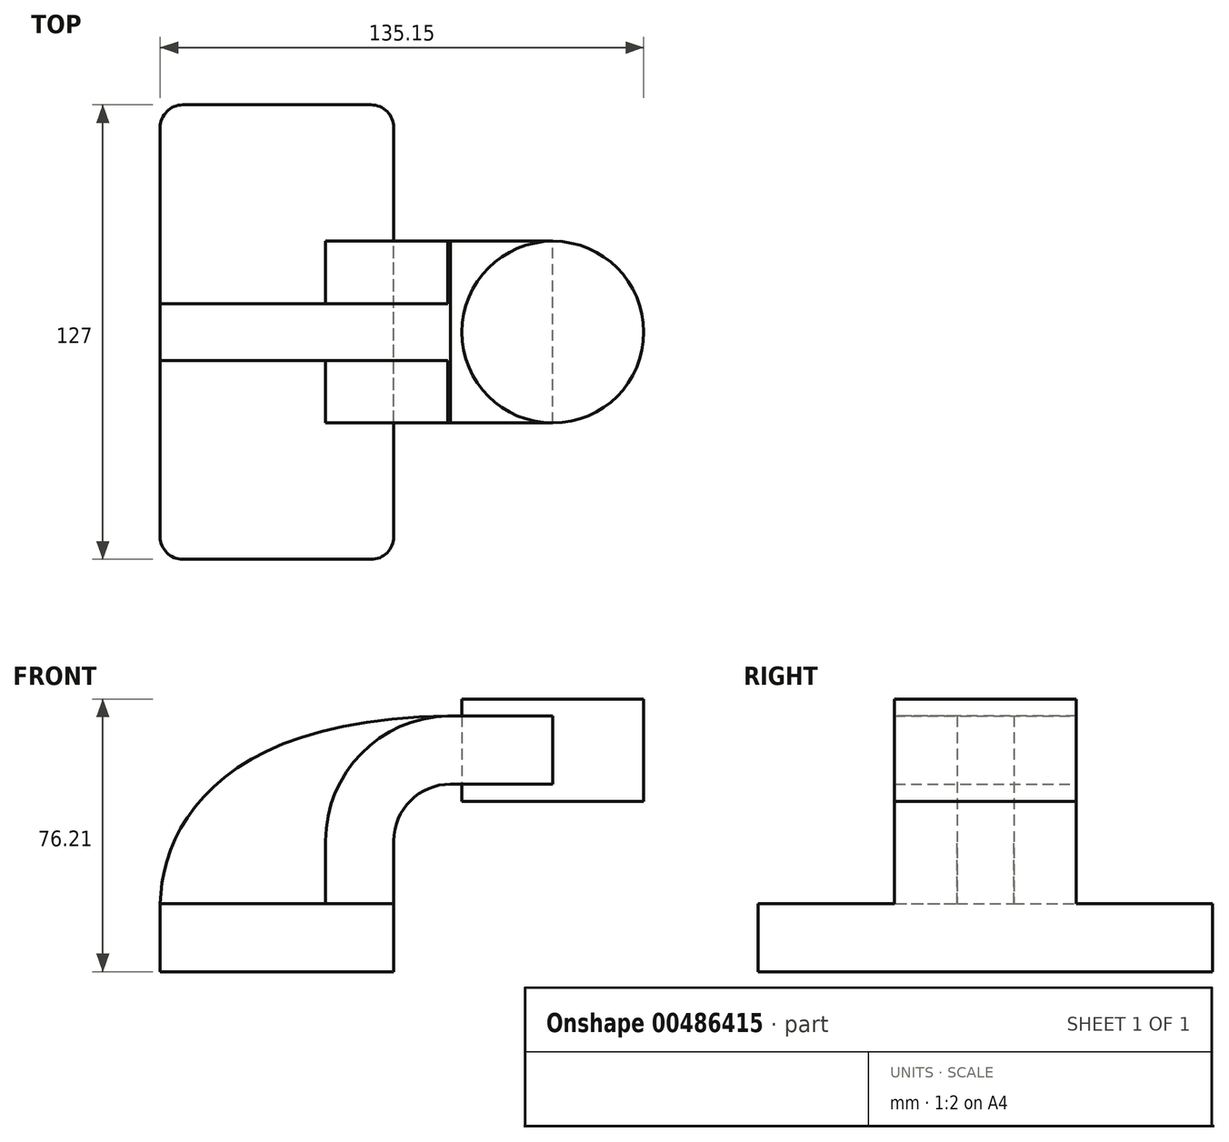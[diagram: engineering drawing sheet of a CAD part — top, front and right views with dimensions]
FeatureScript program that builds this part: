
annotation { "Feature Type Name" : "Feature", "Feature Type Description" : "" }
export const myFeature = defineFeature(function(context is Context, id is Id, definition is map)
    precondition{}
    {
        {
            var Q0;
            Q0=qCreatedBy(makeId("Front.planeOp"),FACE);
            var sketch = newSketch(context, id + "F0", { "sketchPlane" : qUnion([Q0])});
            skLineSegment(sketch, "E0.bottom", {"start": v(32.65, -9.52) * mm, "end": v(-32.65, -9.52) * mm});
            skLineSegment(sketch, "E0.top", {"start": v(32.65, 9.53) * mm, "end": v(-32.65, 9.52) * mm});
            skLineSegment(sketch, "E0.left", {"start": v(32.65, -9.52) * mm, "end": v(32.65, 9.53) * mm});
            skLineSegment(sketch, "E0.right", {"start": v(-32.65, -9.52) * mm, "end": v(-32.65, 9.53) * mm});
            skPoint(sketch, "E0.middle", {"position": v(0, 0) * mm});
            skLineSegment(sketch, "E1.bottom", {"start": v(102.5, 38.1) * mm, "end": v(51.7, 38.1) * mm});
            skLineSegment(sketch, "E1.top", {"start": v(102.5, 66.68) * mm, "end": v(51.7, 66.68) * mm});
            skLineSegment(sketch, "E1.left", {"start": v(102.5, 38.1) * mm, "end": v(102.5, 66.68) * mm});
            skLineSegment(sketch, "E1.right", {"start": v(51.7, 38.1) * mm, "end": v(51.7, 66.68) * mm});
            skPoint(sketch, "E1.middle", {"position": v(77.1, 52.39) * mm});
            skLineSegment(sketch, "E2", {"start": v(32.65, 9.53) * mm, "end": v(32.65, 27) * mm});
            skArc(sketch, "E3", {"start": v(48.52, 42.88) * mm, "mid": v(37.3, 38.23) * mm, "end": v(32.65, 27) * mm});
            skLineSegment(sketch, "E4", {"start": v(48.52, 42.88) * mm, "end": v(77.1, 42.88) * mm});
            skPoint(sketch, "E5", {"position": v(77.1, 38.1) * mm});
            skLineSegment(sketch, "E6.0", {"start": v(13.6, 9.53) * mm, "end": v(13.6, 27) * mm});
            skArc(sketch, "E6.1", {"start": v(48.52, 61.93) * mm, "mid": v(23.83, 51.7) * mm, "end": v(13.6, 27) * mm});
            skLineSegment(sketch, "E6.2", {"start": v(48.52, 61.93) * mm, "end": v(77.1, 61.93) * mm});
            skFitSpline(sketch, "E7", {"points": [v(48.52, 61.93) * mm, v(-32.65, 9.52) * mm], "startDerivative": vector(-194.04, -1.8) * mm, "endDerivative": vector(-2.1, -64.97) * mm});
            skLineSegment(sketch, "E8", {"start": v(77.1, 42.88) * mm, "end": v(77.1, 61.93) * mm});
            skLineSegment(sketch, "E9", {"start": v(77.1, 61.93) * mm, "end": v(77.1, 66.68) * mm});
            skLineSegment(sketch, "E10", {"start": v(77.1, 42.88) * mm, "end": v(77.1, 38.1) * mm});
            skSolve(sketch);
        }
        {
            var Q0;
            Q0=makeQuery(id+"F0.imprint","IMPRINT",FACE,{"disambiguationData":[TD([[makeQuery(id+"F0.imprint","IMPRINT",EDGE,{"derivedFrom":sQuery(id+"F0.wireOp",EDGE,"E0.bottom")}),-1.0]])]});
            var Q1;
            Q1=sQuery(id+"F0.wireOp",EDGE,"E0.bottom");
            var Q2;
            Q2=sQuery(id+"F0.wireOp",EDGE,"E0.left");
            var Q3;
            Q3=sQuery(id+"F0.wireOp",EDGE,"E0.right");
            var Q4;
            Q4=sQuery(id+"F0.wireOp",EDGE,"E1.bottom");
            var Q5;
            Q5=sQuery(id+"F0.wireOp",EDGE,"E1.top");
            var Q6;
            Q6=sQuery(id+"F0.wireOp",EDGE,"E1.left");
            var Q7;
            Q7=sQuery(id+"F0.wireOp",EDGE,"E1.right");
            var Q8;
            Q8=sQuery(id+"F0.wireOp",EDGE,"E2");
            var Q9;
            Q9=sQuery(id+"F0.wireOp",EDGE,"E3");
            var Q10;
            Q10=sQuery(id+"F0.wireOp",EDGE,"E4");
            var Q11;
            Q11=sQuery(id+"F0.wireOp",EDGE,"E6.0");
            var Q12;
            Q12=sQuery(id+"F0.wireOp",EDGE,"E6.1");
            var Q13;
            Q13=sQuery(id+"F0.wireOp",EDGE,"E6.2");
            var Q14;
            Q14=sQuery(id+"F0.wireOp",EDGE,"E7");
            extrude(context, id + "F1", {"entities" : qUnion([Q0]), "surfaceEntities" : qUnion([Q1, Q2, Q3, Q4, Q5, Q6, Q7, Q8, Q9, Q10, Q11, Q12, Q13, Q14]), "endBound" : BoundingType.SYMMETRIC, "depth" : 127 * mm});
        }
        {
            var Q0;
            {var subQ1=sQuery(id+"F0.wireOp",EDGE,"E2");Q0=makeQuery(id+"F0.imprint","IMPRINT",FACE,{"disambiguationData":[TD([[makeQuery(id+"F0.imprint","IMPRINT",EDGE,{"derivedFrom":subQ1}),1.0]])]});}
            var Q1;
            {var subQ5=sQuery(id+"F0.wireOp",EDGE,"E8");Q1=makeQuery(id+"F0.imprint","IMPRINT",FACE,{"disambiguationData":[TD([[makeQuery(id+"F0.imprint","IMPRINT",EDGE,{"derivedFrom":subQ5}),1.0]])]});}
            extrude(context, id + "F2", {"entities" : qUnion([Q0, Q1]), "operationType" : NewBodyOperationType.ADD, "endBound" : BoundingType.SYMMETRIC, "depth" : 50.8 * mm});
        }
        {
            var Q0;
            {var subQ3=sQuery(id+"F0.wireOp",EDGE,"E6.0");Q0=makeQuery(id+"F0.imprint","IMPRINT",FACE,{"disambiguationData":[TD([[makeQuery(id+"F0.imprint","IMPRINT",EDGE,{"derivedFrom":subQ3}),1.0]])]});}
            extrude(context, id + "F3", {"entities" : qUnion([Q0]), "operationType" : NewBodyOperationType.ADD, "endBound" : BoundingType.SYMMETRIC, "depth" : 15.88 * mm});
        }
        {
            var Q0;
            {var subQ0=sQuery(id+"F0.wireOp",EDGE,"E1.left");Q0=makeQuery(id+"F0.imprint","IMPRINT",FACE,{"disambiguationData":[TD([[makeQuery(id+"F0.imprint","IMPRINT",EDGE,{"derivedFrom":subQ0}),1.0]])]});}
            var Q1;
            Q1=sQuery(id+"F0.wireOp",EDGE,"E8");
            revolve(context, id + "F4", {"entities" : qUnion([Q0]), "axis" : qUnion([Q1]), "revolveType" : RevolveType.FULL});
        }
        {
            var Q0;
            Q0=makeQuery(id+"F1.opExtrude","CAP_EDGE",EDGE,{"disambiguationData":[OSD([sQuery(id+"F0.wireOp",EDGE,"E0.right")])],"isStart":false});
            var Q1;
            Q1=makeQuery(id+"F1.opExtrude","CAP_EDGE",EDGE,{"disambiguationData":[OSD([sQuery(id+"F0.wireOp",EDGE,"E0.left")])],"isStart":false});
            var Q2;
            Q2=makeQuery(id+"F1.opExtrude","CAP_EDGE",EDGE,{"disambiguationData":[OSD([sQuery(id+"F0.wireOp",EDGE,"E0.left")])],"isStart":true});
            var Q3;
            Q3=makeQuery(id+"F1.opExtrude","CAP_EDGE",EDGE,{"disambiguationData":[OSD([sQuery(id+"F0.wireOp",EDGE,"E0.right")])],"isStart":true});
            fillet(context, id + "F5", {"entities" : qUnion([Q0, Q1, Q2, Q3]), "radius" : 6.35 * mm, "tangentPropagation" : true, "allowEdgeOverflow" : false});
        }
    });
